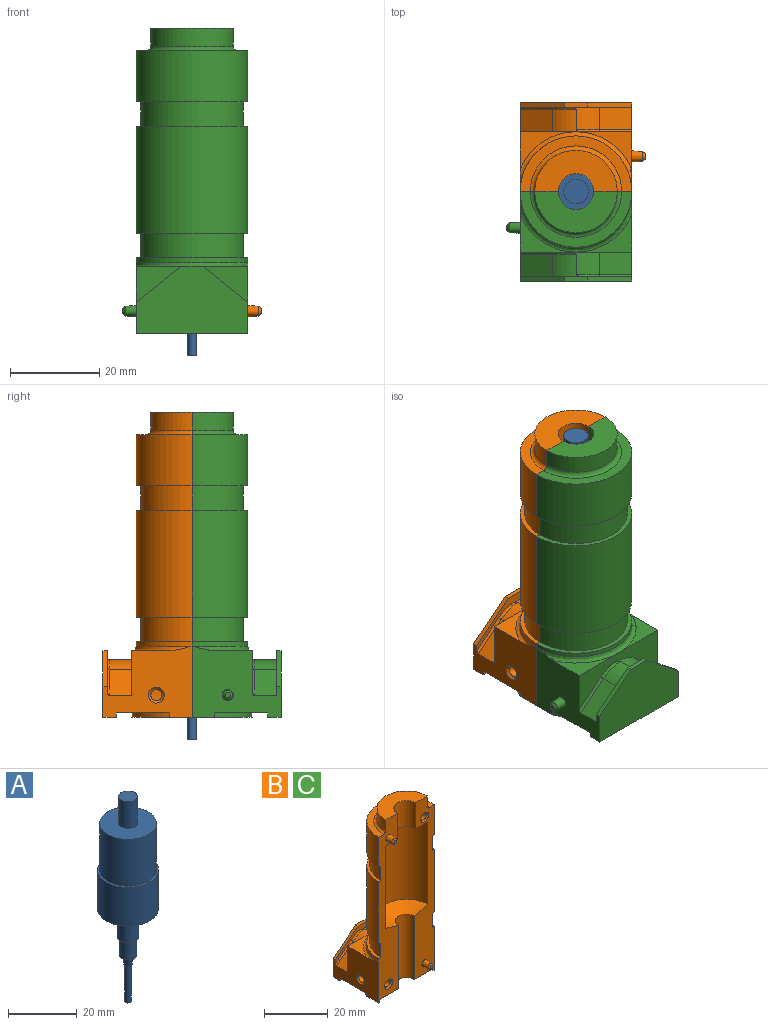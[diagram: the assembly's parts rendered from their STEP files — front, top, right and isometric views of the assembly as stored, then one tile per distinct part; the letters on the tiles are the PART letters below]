
ASSEMBLY  parts=3 mates=2
PART A: 20 faces, bbox 17.8x17.8x73 mm
  f0: cylinder r=8.25mm len=16.7mm, axis (0,0,-1), area 865.7mm2, adj f1,f12
  f1: plane 16.5x16.5mm, normal (0,0,1), area 190.1mm2, adj f0,f2
  f2: cylinder r=2.75mm len=9.5mm, axis (0,0,-1), area 164.1mm2, adj f1,f3
  f3: plane 5.5x5.5mm, normal (0,0,1), area 23.8mm2, adj f2
  f4: plane 2.4x2.4mm, normal (0,0,-1), area 1.4mm2, adj f5,f14
  f5: cone r=1.2mm half-angle=8.1deg, axis (0,0,1), area 32.2mm2, adj f4,f6
  f6: plane 5x5mm, normal (0,0,-1), area 10.6mm2, adj f5,f7
  f7: cylinder r=2.5mm len=6mm, axis (0,0,-1), area 94.2mm2, adj f6,f13
  f8: plane 6.2x6.2mm, normal (0,0,-1), area 1.9mm2, adj f9,f13
  f9: cylinder r=3.1mm len=7.9mm, axis (0,0,-1), area 153.9mm2, adj f8,f10
  f10: cone r=8.9mm half-angle=70.1deg, axis (0,0,1), area 232.5mm2, adj f9,f11
  f11: cylinder r=8.9mm len=17.8mm, axis (0,0,-1), area 771.7mm2, adj f10,f12
  f12: plane 17.8x17.8mm, normal (0,0,1), area 35mm2, adj f0,f11
  f13: cone r=2.5mm half-angle=45deg, axis (0,0,1), area 12.2mm2, adj f7,f8
  f14: cylinder r=1mm len=13mm, axis (0,0,1), area 81.7mm2, adj f4,f15
  f15: plane 2x2mm, normal (0,0,-1), area 1.4mm2, adj f14,f19
  f16: plane 3x3mm, normal (0,0,-1), area 7.1mm2, adj f17
  f17: cylinder r=1.5mm len=14.75mm, axis (0,0,-1), area 139mm2, adj f16,f18
  f18: cone r=1.5mm half-angle=8.1deg, axis (0,0,1), area 37.5mm2, adj f17,f19
  f19: cylinder r=0.75mm len=14mm, axis (0,0,-1), area 66mm2, adj f15,f18
PART B: 65 faces, bbox 31.1x23.2x68.7 mm
  f0: plane 68.5x9mm, normal (0,-1,0), area 375.7mm2, adj f2,f4,f5,f9,f10,f11,f12,f13
  f1: plane 20.19x16.19mm, normal (-1,0,0), area 217.2mm2, adj f2,f3,f6,f7,f19,f21,f22,f31
  f2: plane 25x13.5mm, normal (0,0,-1), area 45.6mm2, adj f0,f1,f6,f18,f60,f64
  f3: plane 25x3mm, normal (0,0,-1), area 75mm2, adj f1,f18,f19,f59
  f4: cylinder r=12.5mm len=25mm, axis (0,0,-1), area 942.5mm2, adj f0,f6,f41,f46
  f5: cylinder r=12.5mm len=25mm, axis (0,0,-1), area 39.3mm2, adj f0,f6,f39,f43
  f6: plane 68.5x9mm, normal (0,-1,0), area 375.7mm2, adj f1,f2,f4,f5,f9,f10,f11,f12
  f7: plane 12.5x8.4mm, normal (0,0,1), area 29mm2, adj f1,f22,f39
  f8: plane 12.5x8.4mm, normal (0,0,1), area 29mm2, adj f18,f22,f39
  f9: cylinder r=12.5mm len=25mm, axis (0,0,-1), area 451.6mm2, adj f0,f6,f13,f44
  f10: cylinder r=9.25mm len=31.5mm, axis (0,0,-1), area 915.4mm2, adj f0,f6,f11,f17
  f11: cone r=3.5mm half-angle=73.5deg, axis (0,0,1), area 120.1mm2, adj f0,f6,f10,f12
  f12: cylinder r=3.5mm len=24.3mm, axis (0,0,-1), area 267.2mm2, adj f0,f6,f11,f63
  f13: plane 25x12.5mm, normal (0,0,1), area 80.4mm2, adj f0,f6,f9,f40
  f14: cylinder r=9.25mm len=18.5mm, axis (0,0,-1), area 116.2mm2, adj f0,f6,f15,f40
  f15: plane 18.5x9.25mm, normal (0,0,1), area 109.3mm2, adj f0,f6,f14,f16
  f16: cylinder r=4mm len=10mm, axis (0,0,-1), area 125.7mm2, adj f0,f6,f15,f17
  f17: plane 18.5x9.25mm, normal (0,0,-1), area 109.3mm2, adj f0,f6,f10,f16
  f18: plane 20.19x16.19mm, normal (1,0,0), area 222.2mm2, adj f0,f2,f3,f8,f19,f21,f22,f32
  f19: plane 25x15mm, normal (0,1,0), area 295mm2, adj f1,f3,f18,f20,f57,f58
  f20: plane 5x1mm, normal (0,0,1), area 5mm2, adj f19,f21,f57,f58
  f21: plane 25x10mm, normal (0,-1,0), area 45.8mm2, adj f1,f18,f20,f32,f33,f37,f38,f57
  f22: plane 25x10mm, normal (0,1,0), area 125.8mm2, adj f1,f7,f8,f18,f31,f34,f35,f36
  f23: cone r=1.25mm half-angle=3deg, axis (0,1,0), area 18.6mm2, adj f6,f50
  f24: plane 1.19x1.19mm, normal (0,-1,0), area 1.1mm2, adj f50
  f25: cone r=1.25mm half-angle=3deg, axis (0,1,0), area 18.6mm2, adj f0,f49
  f26: plane 1.19x1.19mm, normal (0,-1,0), area 1.1mm2, adj f49
  f27: cylinder r=1.25mm len=3mm, axis (0,-1,0), area 23.6mm2, adj f28,f47
  f28: plane 2.5x2.5mm, normal (0,-1,0), area 4.9mm2, adj f27
  f29: cylinder r=1.25mm len=3mm, axis (0,-1,0), area 23.6mm2, adj f30,f48
  f30: plane 2.5x2.5mm, normal (0,-1,0), area 4.9mm2, adj f29
  f31: plane 7.26x5.81mm, normal (-0.62,0,0.78), area 46.5mm2, adj f1,f22,f34,f37
  f32: plane 7.26x5.81mm, normal (0.62,0,0.78), area 46.5mm2, adj f18,f21,f33,f35
  f33: cylinder r=10mm len=7.78mm, axis (0,1,0), area 29mm2, adj f21,f32,f34,f36,f38
  f34: cylinder r=10mm len=7.78mm, axis (0,1,0), area 29mm2, adj f22,f31,f33,f36,f38
  f35: cylinder r=0.5mm len=7.57mm, axis (-0.78,0,0.62), area 7.1mm2, adj f18,f22,f32,f36
  f36: torus R=10.5mm, axis (0,-1,0), area 3.9mm2, adj f22,f33,f34,f35
  f37: cylinder r=0.5mm len=7.57mm, axis (0.78,0,0.62), area 7.1mm2, adj f1,f21,f31,f38
  f38: torus R=10.5mm, axis (0,-1,0), area 3.9mm2, adj f21,f33,f34,f37
  f39: torus R=13.5mm, axis (0,0,-1), area 55.5mm2, adj f1,f5,f7,f8,f18
  f40: torus R=10.25mm, axis (0,0,-1), area 47.4mm2, adj f0,f6,f13,f14
  f41: plane 25x12.5mm, normal (0,0,-1), area 37.7mm2, adj f0,f4,f6,f42
  f42: cylinder r=11.5mm len=23mm, axis (0,0,1), area 198.7mm2, adj f0,f6,f41,f43
  f43: plane 25x12.5mm, normal (0,0,1), area 37.7mm2, adj f0,f5,f6,f42
  f44: plane 25x12.5mm, normal (0,0,-1), area 37.7mm2, adj f0,f6,f9,f45
  f45: cylinder r=11.5mm len=23mm, axis (0,0,1), area 198.7mm2, adj f0,f6,f44,f46
  f46: plane 25x12.5mm, normal (0,0,1), area 37.7mm2, adj f0,f4,f6,f45
  f47: cone r=1.75mm half-angle=45deg, axis (0,-1,0), area 6.7mm2, adj f0,f27
  f48: cone r=1.75mm half-angle=45deg, axis (0,-1,0), area 6.7mm2, adj f6,f29
  f49: cone r=0.59mm half-angle=46.5deg, axis (0,1,0), area 3.9mm2, adj f25,f26
  f50: cone r=0.59mm half-angle=46.5deg, axis (0,1,0), area 3.9mm2, adj f23,f24
  f51: cone r=1.25mm half-angle=3deg, axis (-1,0,0), area 18.6mm2, adj f18,f56
  f52: plane 1.19x1.19mm, normal (1,0,0), area 1.1mm2, adj f56
  f53: cylinder r=1.25mm len=2.97mm, axis (-1,0,0), area 23.4mm2, adj f54,f55
  f54: plane 2.5x2.5mm, normal (-1,0,0), area 4.9mm2, adj f53
  f55: cone r=1.25mm half-angle=45deg, axis (-1,0,0), area 7.1mm2, adj f1,f53
  f56: cone r=0.59mm half-angle=46.5deg, axis (-1,0,0), area 3.9mm2, adj f51,f52
  f57: plane 10x8mm, normal (-0.62,0,0.78), area 12.8mm2, adj f1,f19,f20,f21
  f58: plane 10x8mm, normal (0.62,0,0.78), area 12.8mm2, adj f18,f19,f20,f21
  f59: plane 25x1mm, normal (0,-1,0), area 25mm2, adj f1,f3,f18,f61
  f60: cylinder r=13.5mm len=25mm, axis (0,0,-1), area 32mm2, adj f1,f2,f18,f61
  f61: plane 25x11.9mm, normal (0,0,-1), area 145.6mm2, adj f1,f18,f59,f60
  f62: cylinder r=11.5mm len=23mm, axis (0,0,-1), area 10.8mm2, adj f0,f6,f63,f64
  f63: plane 23x11.5mm, normal (0,0,-1), area 188.5mm2, adj f0,f6,f12,f62
  f64: cone r=11.5mm half-angle=45deg, axis (0,0,-1), area 36.9mm2, adj f0,f2,f6,f62
PART C: same geometry as B
PLACE A t=(0.06,-0.03,-30.03)mm fixed
PLACE B t=(0.06,-0.03,-8)mm
PLACE C rot(axis=(0,0,-1),180deg) t=(0.06,-0.03,-8)mm
MATE planar C.f6 <-> B.f0  axis (0,1,0) through (4.06,-0.03,30.47)mm
MATE revolute A.f0 <-> B.f4  axis (0,0,-1) through (0.06,-0.03,20.47)mm
